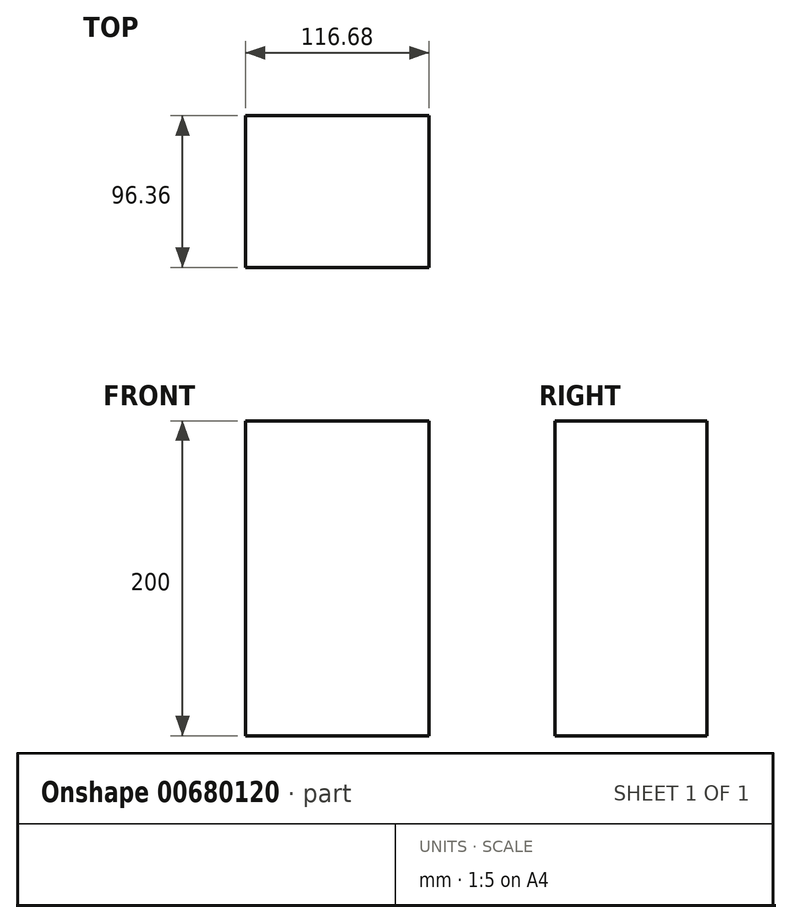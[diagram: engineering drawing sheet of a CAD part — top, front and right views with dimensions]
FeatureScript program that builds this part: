
annotation { "Feature Type Name" : "Feature", "Feature Type Description" : "" }
export const myFeature = defineFeature(function(context is Context, id is Id, definition is map)
    precondition{}
    {
        {
            var Q0;
            Q0=qCreatedBy(makeId("Top.planeOp"),FACE);
            var sketch = newSketch(context, id + "F0", { "sketchPlane" : qUnion([Q0])});
            skLineSegment(sketch, "E0.bottom", {"start": v(58.34, -48.18) * mm, "end": v(-58.34, -48.18) * mm});
            skLineSegment(sketch, "E0.top", {"start": v(58.34, 48.18) * mm, "end": v(-58.34, 48.18) * mm});
            skLineSegment(sketch, "E0.left", {"start": v(58.34, -48.18) * mm, "end": v(58.34, 48.18) * mm});
            skLineSegment(sketch, "E0.right", {"start": v(-58.34, -48.18) * mm, "end": v(-58.34, 48.18) * mm});
            skPoint(sketch, "E0.middle", {"position": v(0, 0) * mm});
            skSolve(sketch);
        }
        {
            var Q0;
            Q0=makeQuery(id+"F0.imprint","IMPRINT",FACE,{"disambiguationData":[TD([[makeQuery(id+"F0.imprint","IMPRINT",EDGE,{"derivedFrom":sQuery(id+"F0.wireOp",EDGE,"E0.bottom")}),-1.0]])]});
            extrude(context, id + "F1", {"entities" : qUnion([Q0]), "depth" : 200 * mm, "offsetDistance" : 25 * mm});
        }
    });
